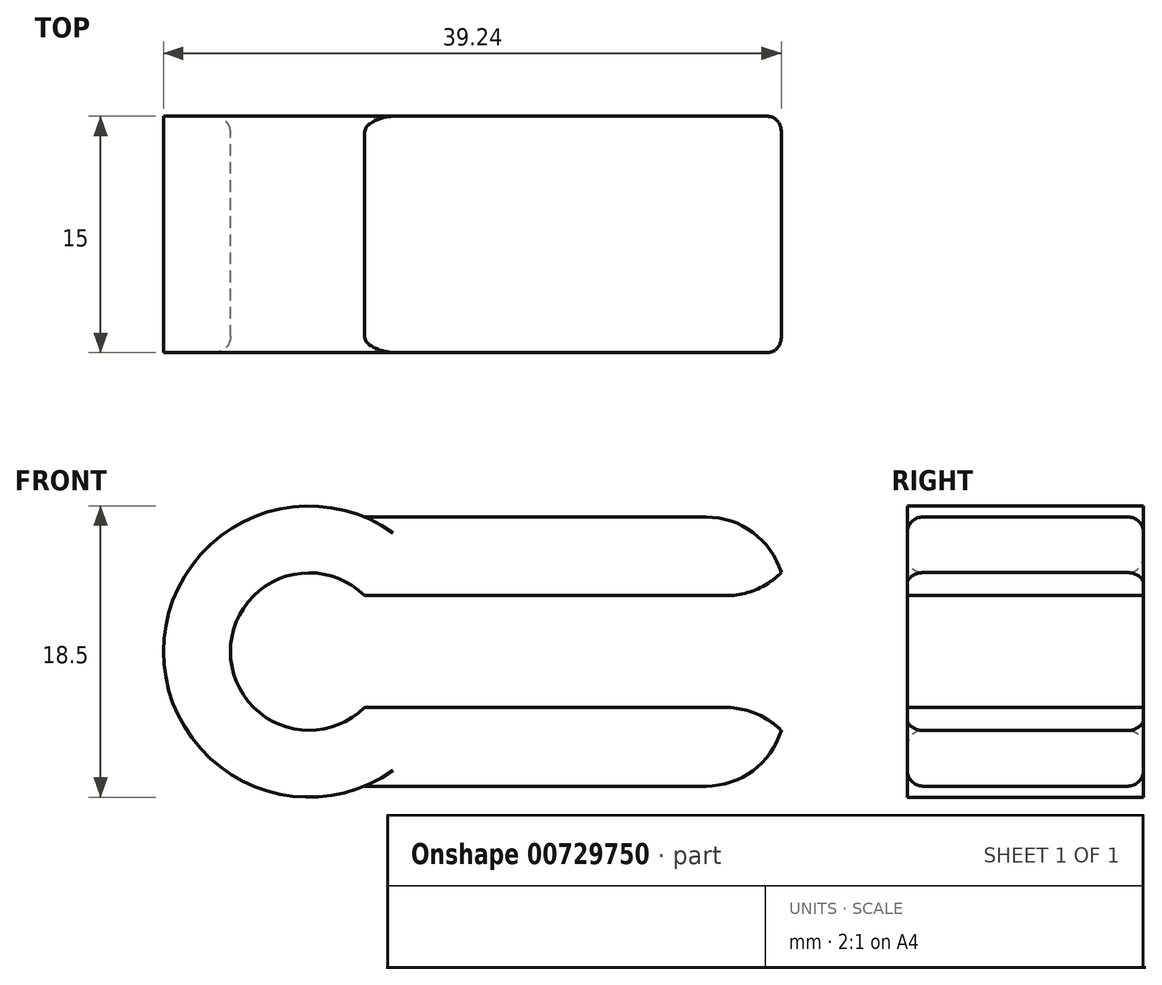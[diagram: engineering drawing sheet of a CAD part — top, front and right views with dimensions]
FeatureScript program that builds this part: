
annotation { "Feature Type Name" : "Feature", "Feature Type Description" : "" }
export const myFeature = defineFeature(function(context is Context, id is Id, definition is map)
    precondition{}
    {
        {
            var Q0;
            Q0=qCreatedBy(makeId("Front.planeOp"),FACE);
            var sketch = newSketch(context, id + "F0", { "sketchPlane" : qUnion([Q0])});
            skArc(sketch, "E0", {"start": v(0.52, 8.55) * mm, "mid": v(-12.25, 0) * mm, "end": v(0.52, -8.55) * mm});
            skArc(sketch, "E1", {"start": v(0.52, 3.55) * mm, "mid": v(-8, 0) * mm, "end": v(0.52, -3.55) * mm});
            skLineSegment(sketch, "E2", {"start": v(0.52, 3.55) * mm, "end": v(23.45, 3.55) * mm});
            skLineSegment(sketch, "E3", {"start": v(0.52, 8.55) * mm, "end": v(30.52, 8.55) * mm});
            skLineSegment(sketch, "E4", {"start": v(0.52, -3.55) * mm, "end": v(23.45, -3.55) * mm});
            skLineSegment(sketch, "E5", {"start": v(0.52, -8.55) * mm, "end": v(30.52, -8.55) * mm});
            skLineSegment(sketch, "E6", {"start": v(26.99, 5.01) * mm, "end": v(30.52, 8.55) * mm});
            skLineSegment(sketch, "E7", {"start": v(26.99, -5.01) * mm, "end": v(30.52, -8.55) * mm});
            skPoint(sketch, "E8.visualSharp", {"position": v(25.52, 3.55) * mm});
            skArc(sketch, "E8.filletArc", {"start": v(23.45, 3.55) * mm, "mid": v(25.36, 3.93) * mm, "end": v(26.99, 5.01) * mm});
            skPoint(sketch, "E9.visualSharp", {"position": v(25.52, -3.55) * mm});
            skArc(sketch, "E9.filletArc", {"start": v(26.99, -5.01) * mm, "mid": v(25.36, -3.93) * mm, "end": v(23.45, -3.55) * mm});
            skSolve(sketch);
        }
        {
            var Q0;
            Q0 = qSketchRegion(id + "F0", true);
            extrude(context, id + "F1", {"entities" : qUnion([Q0]), "depth" : 15 * mm, "offsetDistance" : 25 * mm});
        }
        {
            var Q0;
            Q0=makeQuery(id+"F1.opExtrude","SWEPT_EDGE",EDGE,{"disambiguationData":[OSD([sQuery(id+"F0.wireOp",EDGE,"E5"),sQuery(id+"F0.wireOp",EDGE,"E7")])]});
            var Q1;
            Q1=makeQuery(id+"F1.opExtrude","SWEPT_EDGE",EDGE,{"disambiguationData":[OSD([sQuery(id+"F0.wireOp",EDGE,"E3"),sQuery(id+"F0.wireOp",EDGE,"E6")])]});
            fillet(context, id + "F2", {"entities" : qUnion([Q0, Q1]), "radius" : 5 * mm, "tangentPropagation" : true, "allowEdgeOverflow" : false});
        }
        {
            var Q0;
            Q0=makeQuery(id+"F1.opExtrude","CAP_EDGE",EDGE,{"disambiguationData":[OSD([sQuery(id+"F0.wireOp",EDGE,"E5")])],"isStart":true});
            var Q1;
            Q1=makeQuery(id+"F1.opExtrude","CAP_EDGE",EDGE,{"disambiguationData":[OSD([sQuery(id+"F0.wireOp",EDGE,"E5")])],"isStart":false});
            var Q2;
            Q2=makeQuery(id+"F1.opExtrude","CAP_EDGE",EDGE,{"disambiguationData":[OSD([sQuery(id+"F0.wireOp",EDGE,"E3")])],"isStart":false});
            var Q3;
            Q3=makeQuery(id+"F1.opExtrude","CAP_EDGE",EDGE,{"disambiguationData":[OSD([sQuery(id+"F0.wireOp",EDGE,"E3")])],"isStart":true});
            var Q4;
            Q4=makeQuery(id+"F1.opExtrude","CAP_EDGE",EDGE,{"disambiguationData":[OSD([sQuery(id+"F0.wireOp",EDGE,"E1")])],"isStart":false});
            var Q5;
            Q5=makeQuery(id+"F1.opExtrude","CAP_EDGE",EDGE,{"disambiguationData":[OSD([sQuery(id+"F0.wireOp",EDGE,"E1")])],"isStart":true});
            fillet(context, id + "F3", {"entities" : qUnion([Q0, Q1, Q2, Q3, Q4, Q5]), "radius" : 1 * mm, "tangentPropagation" : true, "allowEdgeOverflow" : false});
        }
    });
